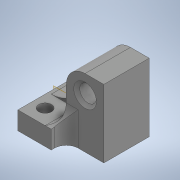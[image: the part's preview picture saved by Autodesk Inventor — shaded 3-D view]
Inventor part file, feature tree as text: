
AUTODESK INVENTOR PART (.ipt)
format: ipt  version: 2022 (Build 260153000, 153)  size: 391,168 bytes
history: native  units: mm
features: extrude x18, sketch x18, reference x11, projected_geometry x9, fillet x5, other x5, chamfer x1, plane x1, mirror x1
ambient origin geometry x8: Origin, YZ Plane, XZ Plane, XY Plane, X Axis, Y Axis, Z Axis, Center Point
bodies: Solid1 (feature_tree)
feature tree (69):
  extrude  "Extrusion1"  Depth=12.1mm
  extrude  "Extrusion2"  Depth=4.0mm TaperAngle=0.0deg
  extrude  "Extrusion3"  Depth=15.0mm
  extrude  "Extrusion4"  Depth=8.0mm
  extrude  "Extrusion5"  Depth=6.0mm TaperAngle=0.0deg
  extrude  "Extrusion6"  Depth=3.0mm
  extrude  "Extrusion7"  Depth=12.4mm
  sketch  "Sketch8"  dims[d23=6.2mm d24=6.2mm]
  extrude  "Extrusion8"  Depth=6.2mm
  extrude  "Extrusion9"  Depth=8.2mm
  fillet  "Fillet1"  Radius=4.0mm
  extrude  "Extrusion10"  Depth=6.2mm
  chamfer  "Chamfer1"  Distance=11.0mm
  extrude  "Extrusion12"  Depth=5.0mm
  fillet  "Fillet2"  Radius=5.0mm
  extrude  "Extrusion13"  Depth=4.2mm
  extrude  "Extrusion14"  Depth=5.0mm
  fillet  "Fillet3"  Radius=11.0mm
  plane  "Work Plane1"
  extrude  "Extrusion15"  Depth=4.0mm TaperAngle=0.0deg
  fillet  "Fillet4"  Radius=2.5mm
  extrude  "Extrusion16"  [1 undecoded]
  extrude  "Extrusion17"  Depth=5.0mm TaperAngle=0.0deg
  mirror  "Mirror1"
  extrude  "Extrusion18"  Depth=5.0mm TaperAngle=0.0deg
  extrude  "Extrusion19"  Depth=5.0mm TaperAngle=0.0deg
  fillet  "Fillet5"  Radius=11.5mm
  sketch  "Sketch1"  dims[d0=11.5mm d1=0.0mm d2=12.1mm]
  reference  "Reference1"
  reference  "Reference2"
  sketch  "Sketch2"  dims[d3=11.5mm d4=0.0mm d5=4.0mm d6=0.0mm]
  sketch  "Sketch3"  dims[d7=2.4mm d8=0.0mm d9=15.0mm]
  reference  "Reference3"
  projected_geometry  "Projected Loop1"
  sketch  "Sketch4"  dims[d12=17.0mm d13=0.0mm d14=8.0mm]
  reference  "Reference4"
  projected_geometry  "Projected Loop2"
  sketch  "Sketch5"  dims[d15=8.0mm d16=6.0mm d17=0.0mm]
  projected_geometry  "Projected Loop3"
  sketch  "Sketch6"  dims[d18=3.0mm d19=3.0mm]
  sketch  "Sketch7"  dims[d20=5.5mm d21=12.4mm]
  sketch  "Sketch9"  dims[d25=27.25mm d26=0.0mm d27=8.2mm d28=4.0mm d29=0.0mm]
  projected_geometry  "Projected Loop4"
  projected_geometry  "Projected Loop5"
  projected_geometry  "Projected Loop6"
  sketch  "Sketch10"  dims[d30=4.0mm d31=0.0mm d32=6.2mm]
  reference  "Reference5"
  reference  "Reference6"
  sketch  "Sketch12"  dims[d33=6.0mm d34=11.0mm d35=0.0mm]
  reference  "Reference9"
  reference  "Reference10"
  sketch  "Sketch13"  dims[d40=1.0mm d41=2.0mm d42=45.0deg d48=5.0mm d49=5.0mm]
  reference  "Reference11"
  sketch  "Sketch14"  dims[d50=8.0mm d51=4.2mm]
  reference  "Reference12"
  reference  "Reference13"
  sketch  "Sketch15"  dims[d52=4.0mm d53=5.0mm d54=11.0mm d55=0.0mm]
  sketch  "Sketch16"  dims[d56=3.9mm d57=4.0mm d58=0.0mm d59=2.5mm d60=0.0mm]
  sketch  "Sketch17"  dims[d61=6.2mm d62=-12.5mm]
  projected_geometry  "Projected Loop7"
  sketch  "Sketch18"  dims[d63=10.0mm d64=5.0mm d65=0.0mm]
  projected_geometry  "Projected Loop8"
  projected_geometry  "Projected Loop9"
  sketch  "Sketch19"  dims[d66=2.0mm d67=18.5mm d68=0.0mm d69=18.5mm d70=0.0mm d71=11.5mm d72=0.0mm d73=2.25mm d74=0.0mm d75=5.0mm]
  other  "toolhead v2.iam"
  other  "Toolplate  V2:1"
  other  "E3D-VOLCANO-1.75-MO:1"
  other  "volcano tool.iam"
  other  "sherpa_mini_release1:1"
note: 1 required parameter value undecoded (feature->parameter linkage not recoverable at this tier; creation-order binding heuristic only, values carry confidence <= 0.55)
